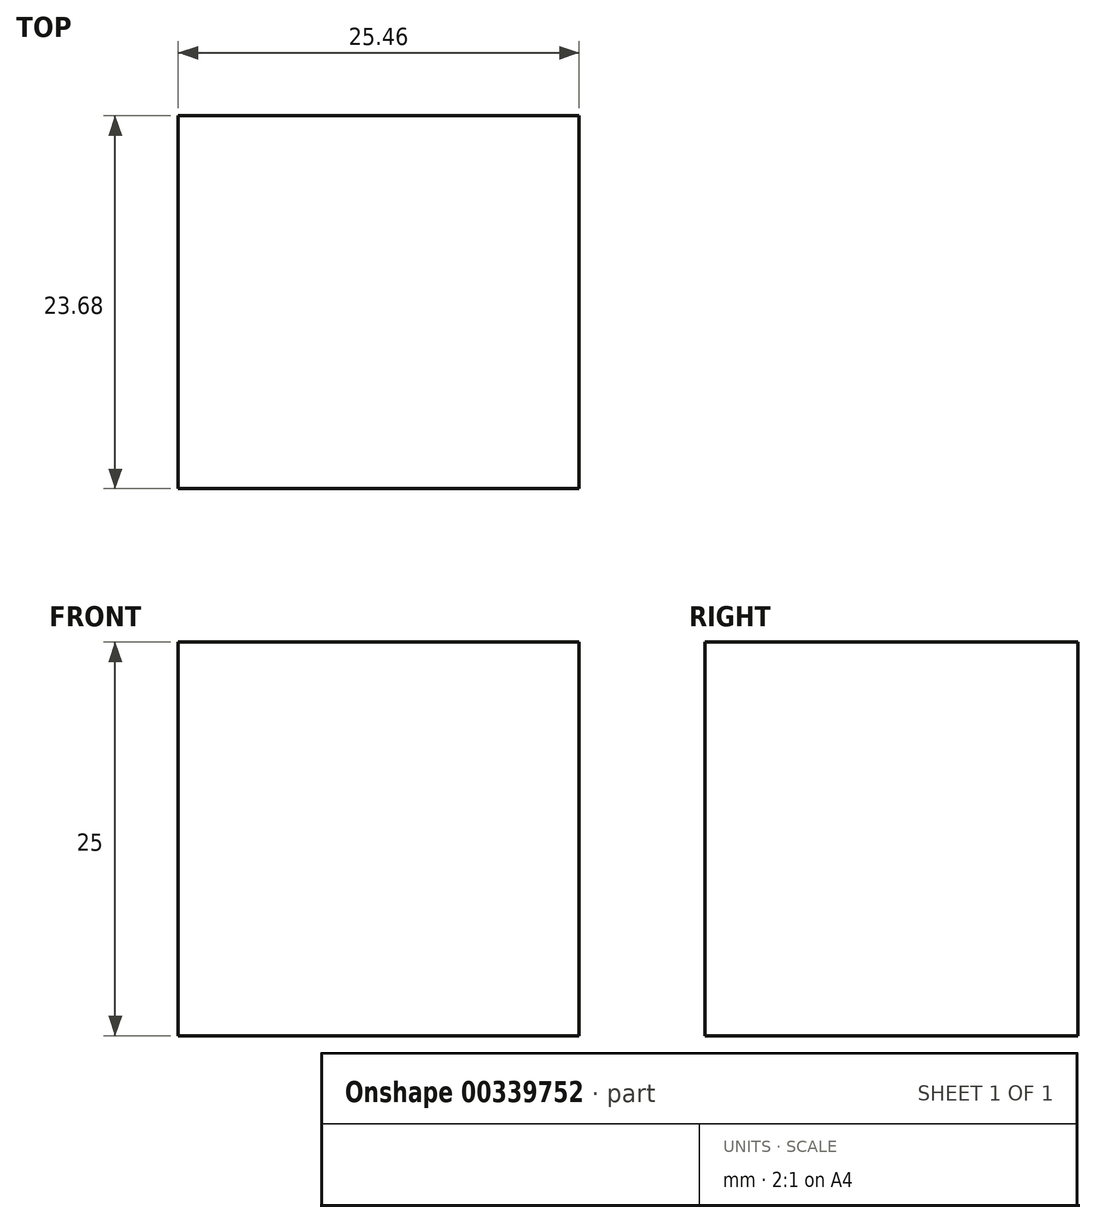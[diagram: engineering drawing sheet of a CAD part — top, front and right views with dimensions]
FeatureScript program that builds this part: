
annotation { "Feature Type Name" : "Feature", "Feature Type Description" : "" }
export const myFeature = defineFeature(function(context is Context, id is Id, definition is map)
    precondition{}
    {
        {
            var Q0;
            Q0=qCreatedBy(makeId("Top.planeOp"),FACE);
            var sketch = newSketch(context, id + "F0", { "sketchPlane" : qUnion([Q0])});
            skLineSegment(sketch, "E0.bottom", {"start": v(12.73, 11.84) * mm, "end": v(-12.73, 11.84) * mm});
            skLineSegment(sketch, "E0.top", {"start": v(12.73, -11.84) * mm, "end": v(-12.73, -11.84) * mm});
            skLineSegment(sketch, "E0.left", {"start": v(12.73, 11.84) * mm, "end": v(12.73, -11.84) * mm});
            skLineSegment(sketch, "E0.right", {"start": v(-12.73, 11.84) * mm, "end": v(-12.73, -11.84) * mm});
            skPoint(sketch, "E0.middle", {"position": v(0, 0) * mm});
            skSolve(sketch);
        }
        {
            var Q0;
            Q0 = qSketchRegion(id + "F0", true);
            extrude(context, id + "F1", {"entities" : qUnion([Q0]), "depth" : 25 * mm});
        }
    });
